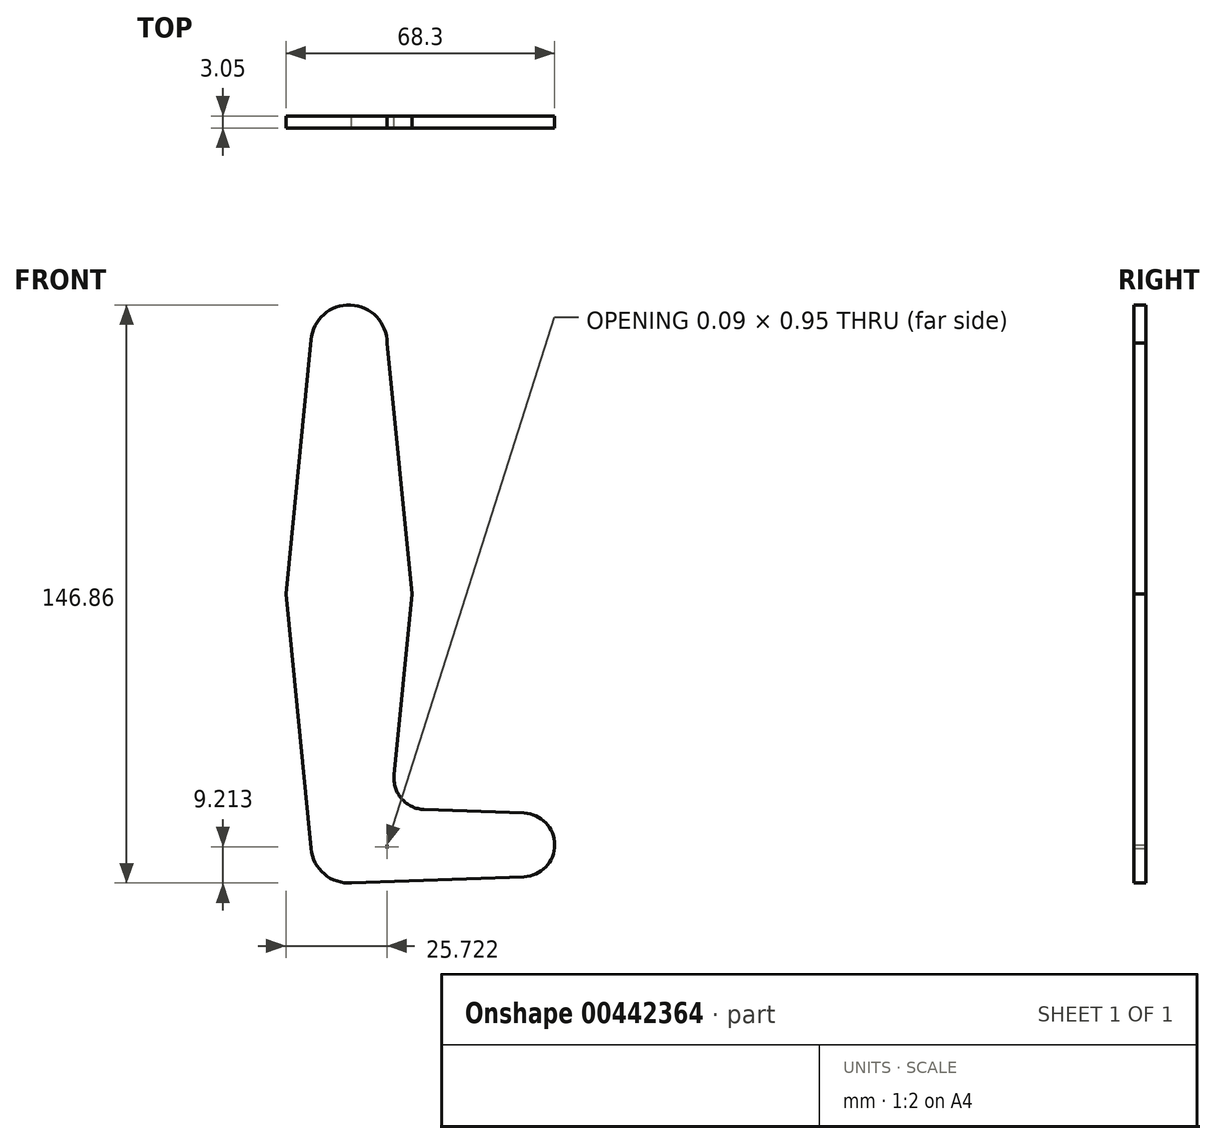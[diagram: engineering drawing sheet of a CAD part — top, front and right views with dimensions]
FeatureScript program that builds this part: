
annotation { "Feature Type Name" : "Feature", "Feature Type Description" : "" }
export const myFeature = defineFeature(function(context is Context, id is Id, definition is map)
    precondition{}
    {
        {
            var Q0;
            Q0=qCreatedBy(makeId("Front.planeOp"),FACE);
            var sketch = newSketch(context, id + "F0", { "sketchPlane" : qUnion([Q0])});
            skCircle(sketch, "E0", {"center": v(0, 0) * mm, "radius": 15.95 * mm});
            skLineSegment(sketch, "E1", {"start": v(0, 0) * mm, "end": v(0, -63.74) * mm});
            skLineSegment(sketch, "E2", {"start": v(0, 0) * mm, "end": v(0, 63.74) * mm});
            skCircle(sketch, "E3", {"center": v(0, 63.74) * mm, "radius": 9.7 * mm});
            skCircle(sketch, "E4.MirrorC", {"center": v(0, -63.74) * mm, "radius": 9.7 * mm});
            skLineSegment(sketch, "E5", {"start": v(0, -63.74) * mm, "end": v(44.2, -63.74) * mm});
            skCircle(sketch, "E6", {"center": v(44.2, -63.74) * mm, "radius": 8.07 * mm});
            skLineSegment(sketch, "E7", {"start": v(-9.64, 64.78) * mm, "end": v(-16.03, 0) * mm});
            skLineSegment(sketch, "E8", {"start": v(9.7, 63.75) * mm, "end": v(16.03, 0) * mm});
            skLineSegment(sketch, "E9", {"start": v(-16.03, 0) * mm, "end": v(-9.65, -64.7) * mm});
            skLineSegment(sketch, "E10.MirrorCS", {"start": v(9.74, -63.74) * mm, "end": v(9.65, -64.7) * mm});
            skPoint(sketch, "E11.orphan", {"position": v(16.03, 0) * mm});
            skLineSegment(sketch, "E12", {"start": v(16.03, 0) * mm, "end": v(11.49, -46.02) * mm});
            skLineSegment(sketch, "E13", {"start": v(19.1, -54.75) * mm, "end": v(44.5, -55.67) * mm});
            skLineSegment(sketch, "E14", {"start": v(0, -73.43) * mm, "end": v(44.5, -71.8) * mm});
            skArc(sketch, "E15.filletArc", {"start": v(11.49, -46.02) * mm, "mid": v(13.41, -52.03) * mm, "end": v(19.1, -54.75) * mm});
            skSolve(sketch);
        }
        {
            var Q0;
            Q0 = qSketchRegion(id + "F0", true);
            var Q1;
            {var subQ0=sQuery(id+"F0.wireOp",EDGE,"E5");var subQ1=sQuery(id+"F0.wireOp",EDGE,"E1");var subQ2=makeQuery(id+"F0.imprint","INTERSECT",VERTEX,{"derivedFrom":[subQ1,subQ0]});Q1=makeQuery(id+"F0.imprint","IMPRINT",FACE,{"disambiguationData":[TD([[makeQuery(id+"F0.imprint","IMPRINT",EDGE,{"disambiguationData":[TD([[subQ2,1.0]])],"derivedFrom":subQ1}),1.0]])]});}
            extrude(context, id + "F1", {"entities" : qUnion([Q0, Q1]), "depth" : 3.05 * mm});
        }
    });
